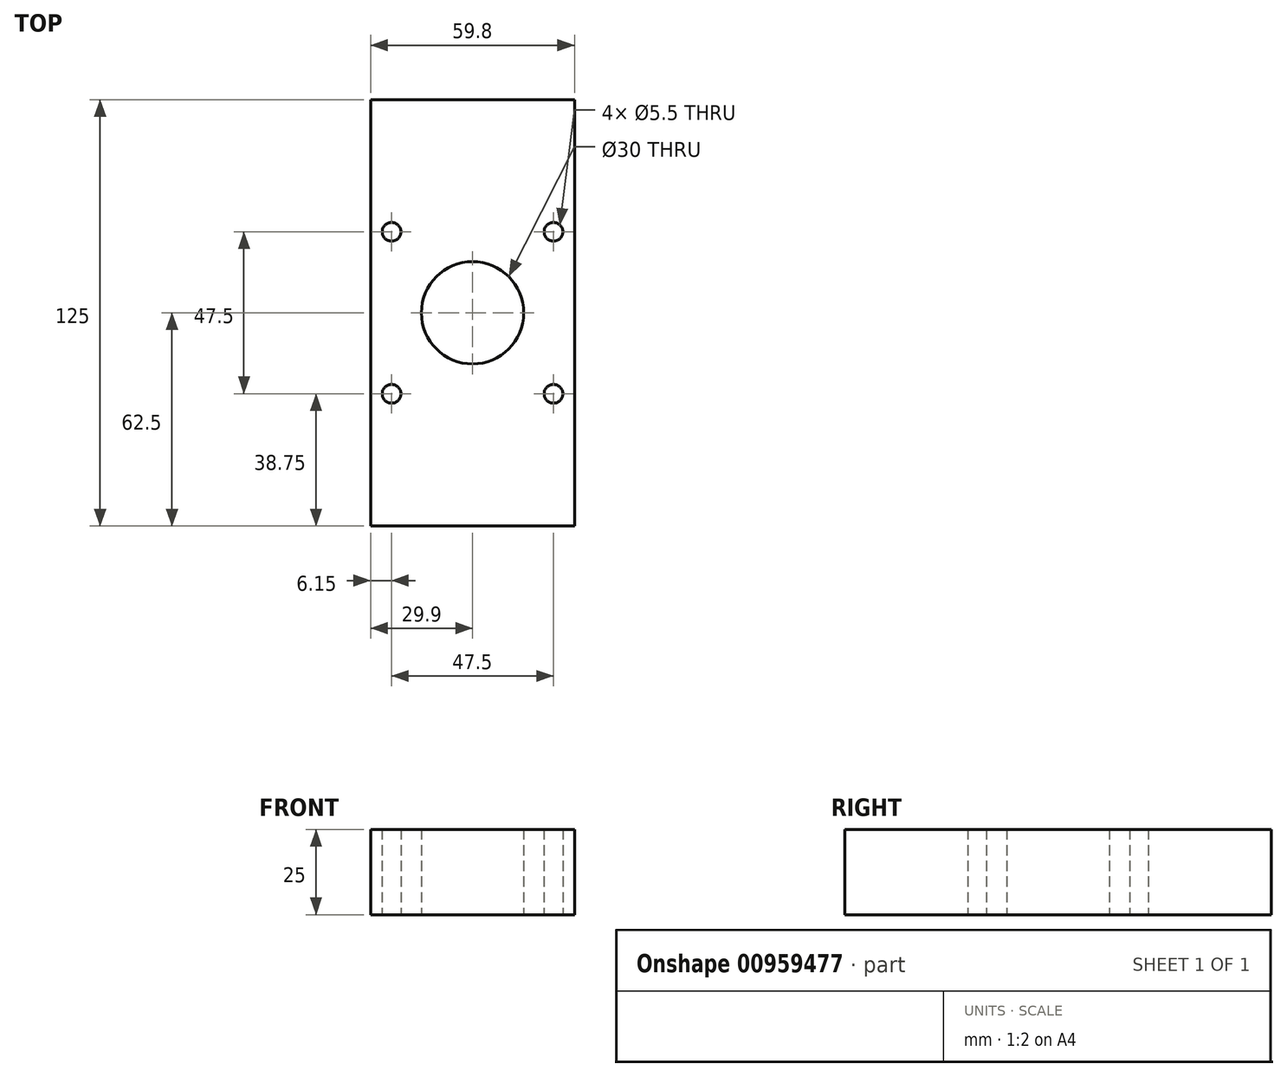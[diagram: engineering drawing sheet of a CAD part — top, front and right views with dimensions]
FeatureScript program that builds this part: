
annotation { "Feature Type Name" : "Feature", "Feature Type Description" : "" }
export const myFeature = defineFeature(function(context is Context, id is Id, definition is map)
    precondition{}
    {
        {
            var Q0;
            Q0=qCreatedBy(makeId("Top.planeOp"),FACE);
            var sketch = newSketch(context, id + "F0", { "sketchPlane" : qUnion([Q0])});
            skLineSegment(sketch, "E0.bottom", {"start": v(-29.9, 62.5) * mm, "end": v(29.9, 62.5) * mm});
            skLineSegment(sketch, "E0.top", {"start": v(-29.9, -62.5) * mm, "end": v(29.9, -62.5) * mm});
            skLineSegment(sketch, "E0.left", {"start": v(-29.9, 62.5) * mm, "end": v(-29.9, -62.5) * mm});
            skLineSegment(sketch, "E0.right", {"start": v(29.9, 62.5) * mm, "end": v(29.9, -62.5) * mm});
            skCircle(sketch, "E1", {"center": v(0, 0) * mm, "radius": 15 * mm});
            skCircle(sketch, "E2", {"center": v(23.75, 23.75) * mm, "radius": 2.75 * mm});
            skCircle(sketch, "E3", {"center": v(23.75, -23.75) * mm, "radius": 2.75 * mm});
            skCircle(sketch, "E4", {"center": v(-23.75, -23.75) * mm, "radius": 2.75 * mm});
            skCircle(sketch, "E5", {"center": v(-23.75, 23.75) * mm, "radius": 2.75 * mm});
            skLineSegment(sketch, "E6", {"start": v(0, 62.5) * mm, "end": v(0, -62.5) * mm, "construction": true});
            skLineSegment(sketch, "E7", {"start": v(-29.9, 0) * mm, "end": v(29.9, 0) * mm, "construction": true});
            skLineSegment(sketch, "E8", {"start": v(-23.75, 23.75) * mm, "end": v(23.75, 23.75) * mm, "construction": true});
            skLineSegment(sketch, "E9", {"start": v(23.75, 23.75) * mm, "end": v(23.75, -23.75) * mm, "construction": true});
            skLineSegment(sketch, "E10", {"start": v(23.75, -23.75) * mm, "end": v(-23.75, -23.75) * mm, "construction": true});
            skLineSegment(sketch, "E11", {"start": v(-23.75, -23.75) * mm, "end": v(-23.75, -62.5) * mm, "construction": true});
            skLineSegment(sketch, "E12", {"start": v(-23.75, -62.5) * mm, "end": v(-23.75, -23.75) * mm, "construction": true});
            skLineSegment(sketch, "E13", {"start": v(-29.9, -23.75) * mm, "end": v(-23.75, -23.75) * mm, "construction": true});
            skLineSegment(sketch, "E14", {"start": v(-23.75, 23.75) * mm, "end": v(-23.75, 62.5) * mm, "construction": true});
            skLineSegment(sketch, "E15", {"start": v(23.75, -23.75) * mm, "end": v(29.9, -23.75) * mm, "construction": true});
            skSolve(sketch);
        }
        {
            var Q0;
            Q0=makeQuery(id+"F0.imprint","IMPRINT",FACE,{"disambiguationData":[TD([[makeQuery(id+"F0.imprint","IMPRINT",EDGE,{"derivedFrom":sQuery(id+"F0.wireOp",EDGE,"E0.bottom")}),-1.0]])]});
            extrude(context, id + "F1", {"entities" : qUnion([Q0]), "depth" : 25 * mm, "offsetDistance" : 25 * mm});
        }
    });
